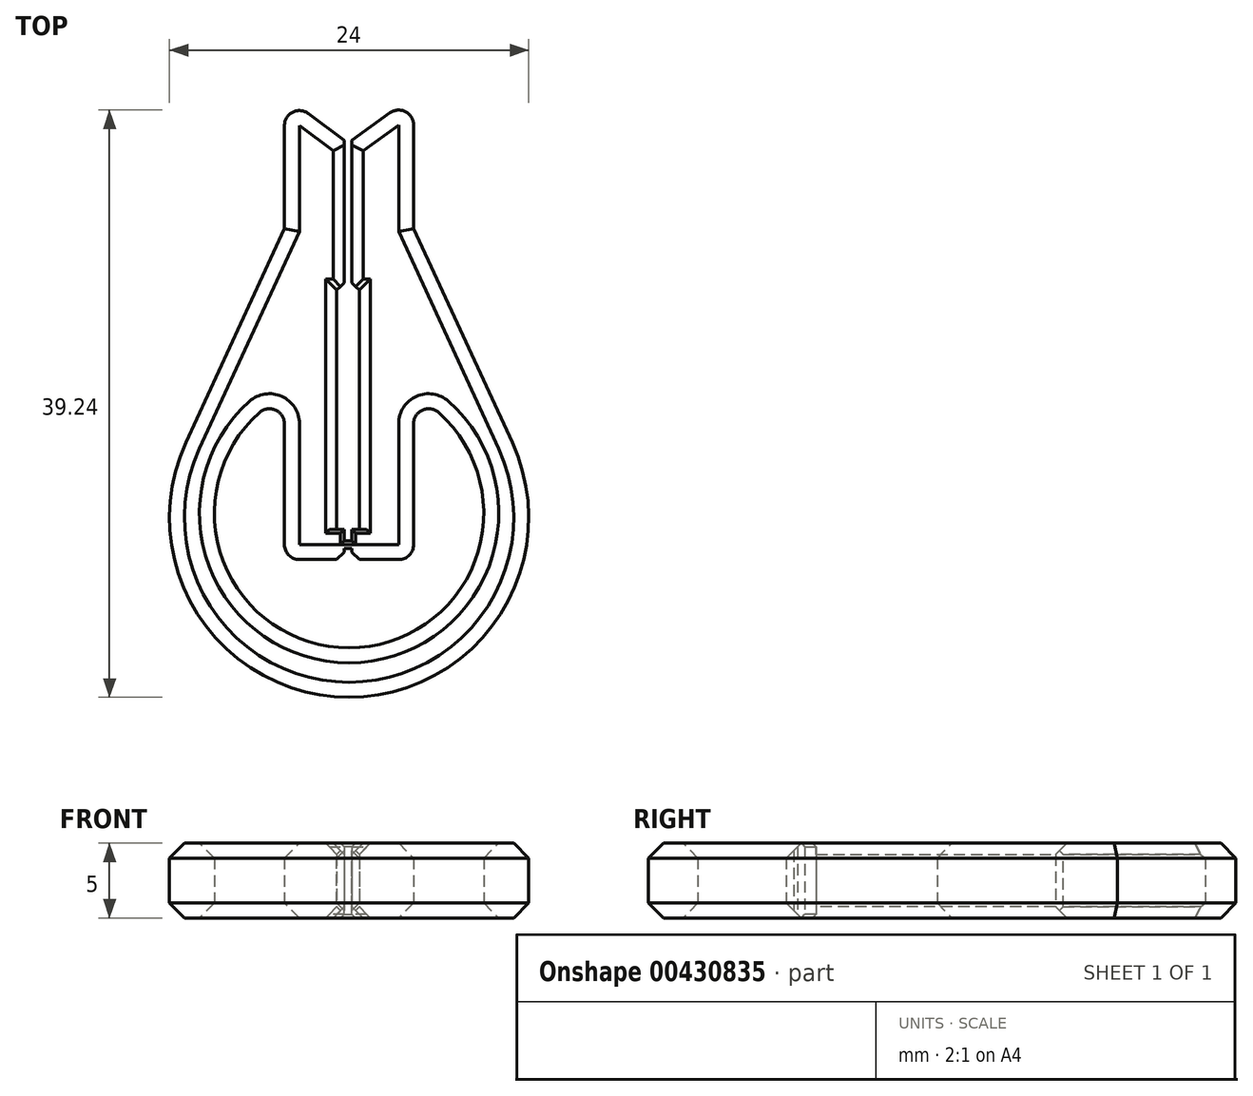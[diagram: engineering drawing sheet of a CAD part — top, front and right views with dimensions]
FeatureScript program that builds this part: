
annotation { "Feature Type Name" : "Feature", "Feature Type Description" : "" }
export const myFeature = defineFeature(function(context is Context, id is Id, definition is map)
    precondition{}
    {
        {
            var Q0;
            Q0=qCreatedBy(makeId("Top.planeOp"),FACE);
            var sketch = newSketch(context, id + "F0", { "sketchPlane" : qUnion([Q0])});
            skLineSegment(sketch, "E0", {"start": v(-0.25, 45.37) * mm, "end": v(-0.25, 35.37) * mm});
            skLineSegment(sketch, "E1", {"start": v(-0.25, 35.37) * mm, "end": v(-0.75, 35.37) * mm});
            skLineSegment(sketch, "E2", {"start": v(-4.25, 17.37) * mm, "end": v(-4.25, 28.37) * mm});
            skLineSegment(sketch, "E3", {"start": v(-4.25, 48.37) * mm, "end": v(-0.25, 45.37) * mm});
            skLineSegment(sketch, "E4", {"start": v(-4.25, 17.37) * mm, "end": v(-0.25, 17.37) * mm});
            skLineSegment(sketch, "E5", {"start": v(-0.25, 17.37) * mm, "end": v(-0.25, 18.12) * mm});
            skLineSegment(sketch, "E6", {"start": v(-0.25, 19.37) * mm, "end": v(-0.75, 19.37) * mm});
            skLineSegment(sketch, "E7", {"start": v(-0.75, 19.37) * mm, "end": v(-0.75, 35.37) * mm});
            skPoint(sketch, "E8", {"position": v(-4.25, 45.37) * mm});
            skPoint(sketch, "E9", {"position": v(-0.25, 18.62) * mm});
            skPoint(sketch, "E10", {"position": v(-0.25, 18.12) * mm});
            skLineSegment(sketch, "E11.MirrorCS", {"start": v(0.25, 19.37) * mm, "end": v(0.75, 19.37) * mm});
            skLineSegment(sketch, "E12.MirrorCS", {"start": v(0.25, 17.37) * mm, "end": v(0.25, 18.12) * mm});
            skPoint(sketch, "E13.MirrorP", {"position": v(0.25, 18.62) * mm});
            skLineSegment(sketch, "E14.MirrorCS", {"start": v(0.25, 35.37) * mm, "end": v(0.75, 35.37) * mm});
            skLineSegment(sketch, "E15.MirrorCS", {"start": v(4.38, 17.37) * mm, "end": v(0.25, 17.37) * mm});
            skPoint(sketch, "E16.MirrorP", {"position": v(0.25, 18.12) * mm});
            skLineSegment(sketch, "E17.MirrorCS", {"start": v(0.75, 19.37) * mm, "end": v(0.75, 35.37) * mm});
            skLineSegment(sketch, "E18.MirrorCS", {"start": v(4.38, 48.37) * mm, "end": v(0.25, 45.37) * mm});
            skLineSegment(sketch, "E19.MirrorCS", {"start": v(4.38, 17.37) * mm, "end": v(4.38, 28.37) * mm});
            skLineSegment(sketch, "E20.MirrorCS", {"start": v(0.25, 45.37) * mm, "end": v(0.25, 35.37) * mm});
            skPoint(sketch, "E21", {"position": v(-4.25, 31.37) * mm});
            skPoint(sketch, "E22", {"position": v(4.38, 31.37) * mm});
            skArc(sketch, "E23", {"start": v(-10.83, 25.2) * mm, "mid": v(0.07, 8.17) * mm, "end": v(10.97, 25.2) * mm});
            skArc(sketch, "E24", {"start": v(-4.25, 28.37) * mm, "mid": v(0.07, 11.47) * mm, "end": v(4.38, 28.37) * mm});
            skLineSegment(sketch, "E25", {"start": v(-4.25, 28.37) * mm, "end": v(4.38, 28.37) * mm, "construction": true});
            skLineSegment(sketch, "E26", {"start": v(-4.25, 31.37) * mm, "end": v(4.38, 31.37) * mm, "construction": true});
            skPoint(sketch, "E27", {"position": v(4.38, 45.37) * mm});
            skLineSegment(sketch, "E28", {"start": v(-0.25, 45.37) * mm, "end": v(0.25, 45.37) * mm, "construction": true});
            skLineSegment(sketch, "E29.trimOffspring", {"start": v(0.25, 18.62) * mm, "end": v(0.25, 19.37) * mm});
            skLineSegment(sketch, "E30.trimOffspring", {"start": v(-0.25, 18.62) * mm, "end": v(-0.25, 19.37) * mm});
            skLineSegment(sketch, "E31", {"start": v(-4.25, 48.37) * mm, "end": v(4.38, 48.37) * mm, "construction": true});
            skLineSegment(sketch, "E32.trimOffspring", {"start": v(-4.25, 31.37) * mm, "end": v(-4.25, 48.37) * mm});
            skLineSegment(sketch, "E33.trimOffspring", {"start": v(4.38, 31.37) * mm, "end": v(4.38, 48.37) * mm});
            skPoint(sketch, "E34", {"position": v(-4.25, 39.5) * mm});
            skPoint(sketch, "E35", {"position": v(4.38, 39.5) * mm});
            skLineSegment(sketch, "E36", {"start": v(-4.25, 39.5) * mm, "end": v(-4.25, 31.37) * mm, "construction": true});
            skLineSegment(sketch, "E37", {"start": v(4.38, 39.5) * mm, "end": v(4.38, 31.37) * mm, "construction": true});
            skLineSegment(sketch, "E38", {"start": v(-4.25, 39.5) * mm, "end": v(-10.83, 25.2) * mm});
            skLineSegment(sketch, "E39", {"start": v(4.38, 39.5) * mm, "end": v(10.97, 25.2) * mm});
            skPoint(sketch, "E40", {"position": v(-10.83, 25.2) * mm});
            skPoint(sketch, "E41", {"position": v(10.97, 25.2) * mm});
            skLineSegment(sketch, "E42", {"start": v(-0.25, 18.62) * mm, "end": v(0, 18.62) * mm});
            skLineSegment(sketch, "E43", {"start": v(-0.25, 18.12) * mm, "end": v(0.25, 18.12) * mm});
            skLineSegment(sketch, "E44", {"start": v(-0.25, 17.37) * mm, "end": v(-0.25, 18.12) * mm, "construction": true});
            skLineSegment(sketch, "E45", {"start": v(-0.25, 19.37) * mm, "end": v(-0.25, 18.62) * mm, "construction": true});
            skLineSegment(sketch, "E46", {"start": v(0, 18.62) * mm, "end": v(0.25, 18.62) * mm});
            skSolve(sketch);
        }
        {
            var Q0;
            Q0=makeQuery(id+"F0.imprint","IMPRINT",FACE,{"disambiguationData":[TD([[makeQuery(id+"F0.imprint","IMPRINT",EDGE,{"derivedFrom":sQuery(id+"F0.wireOp",EDGE,"E0")}),-1.0]])]});
            var Q1;
            Q1=makeQuery(id+"F0.imprint","IMPRINT",FACE,{"disambiguationData":[TD([[makeQuery(id+"F0.imprint","IMPRINT",EDGE,{"derivedFrom":sQuery(id+"F0.wireOp",EDGE,"JaDM6d9C-7Ljt-ahR3-fbqs-DUhw12I5umXE")}),1.0]])]});
            extrude(context, id + "F1", {"entities" : qUnion([Q0, Q1]), "depth" : 5 * mm});
        }
        {
            var Q0;
            Q0=makeQuery(id+"F1.opExtrude","SWEPT_EDGE",EDGE,{"disambiguationData":[OSD([sQuery(id+"F0.wireOp",EDGE,"E3"),sQuery(id+"F0.wireOp",EDGE,"E32.trimOffspring")])]});
            var Q1;
            Q1=makeQuery(id+"F1.opExtrude","SWEPT_EDGE",EDGE,{"disambiguationData":[OSD([sQuery(id+"F0.wireOp",EDGE,"E18.MirrorCS"),sQuery(id+"F0.wireOp",EDGE,"E33.trimOffspring")])]});
            var Q2;
            Q2=makeQuery(id+"F1.opExtrude","SWEPT_EDGE",EDGE,{"disambiguationData":[OSD([sQuery(id+"F0.wireOp",EDGE,"E2"),sQuery(id+"F0.wireOp",EDGE,"E4")])]});
            var Q3;
            Q3=makeQuery(id+"F1.opExtrude","SWEPT_EDGE",EDGE,{"disambiguationData":[OSD([sQuery(id+"F0.wireOp",EDGE,"E15.MirrorCS"),sQuery(id+"F0.wireOp",EDGE,"E19.MirrorCS")])]});
            var Q4;
            Q4=makeQuery(id+"F1.opExtrude","SWEPT_EDGE",EDGE,{"disambiguationData":[OSD([sQuery(id+"F0.wireOp",EDGE,"E19.MirrorCS"),sQuery(id+"F0.wireOp",EDGE,"E24")])]});
            var Q5;
            Q5=makeQuery(id+"F1.opExtrude","SWEPT_EDGE",EDGE,{"disambiguationData":[OSD([sQuery(id+"F0.wireOp",EDGE,"E2"),sQuery(id+"F0.wireOp",EDGE,"E24")])]});
            fillet(context, id + "F2", {"entities" : qUnion([Q0, Q1, Q2, Q3, Q4, Q5]), "radius" : 1 * mm, "tangentPropagation" : true, "allowEdgeOverflow" : false});
        }
        {
            var Q0;
            Q0=makeQuery(id+"F1.opExtrude","CAP_EDGE",EDGE,{"disambiguationData":[OSD([sQuery(id+"F0.wireOp",EDGE,"E43")])],"isStart":false});
            var Q1;
            Q1=makeQuery(id+"F1.opExtrude","CAP_EDGE",EDGE,{"disambiguationData":[OSD([sQuery(id+"F0.wireOp",EDGE,"E42"),sQuery(id+"F0.wireOp",EDGE,"E46")])],"isStart":false});
            var Q2;
            Q2=makeQuery(id+"F1.opExtrude","CAP_EDGE",EDGE,{"disambiguationData":[OSD([sQuery(id+"F0.wireOp",EDGE,"E42"),sQuery(id+"F0.wireOp",EDGE,"E46")])],"isStart":true});
            var Q3;
            Q3=makeQuery(id+"F1.opExtrude","CAP_EDGE",EDGE,{"disambiguationData":[OSD([sQuery(id+"F0.wireOp",EDGE,"E43")])],"isStart":true});
            var Q4;
            Q4=makeQuery(id+"F1.opExtrude","CAP_EDGE",EDGE,{"disambiguationData":[OSD([sQuery(id+"F0.wireOp",EDGE,"E5")])],"isStart":true});
            var Q5;
            Q5=makeQuery(id+"F1.opExtrude","CAP_EDGE",EDGE,{"disambiguationData":[OSD([sQuery(id+"F0.wireOp",EDGE,"E12.MirrorCS")])],"isStart":true});
            var Q6;
            Q6=makeQuery(id+"F1.opExtrude","CAP_EDGE",EDGE,{"disambiguationData":[OSD([sQuery(id+"F0.wireOp",EDGE,"E30.trimOffspring")])],"isStart":true});
            var Q7;
            Q7=makeQuery(id+"F1.opExtrude","CAP_EDGE",EDGE,{"disambiguationData":[OSD([sQuery(id+"F0.wireOp",EDGE,"E29.trimOffspring")])],"isStart":true});
            var Q8;
            Q8=makeQuery(id+"F1.opExtrude","CAP_EDGE",EDGE,{"disambiguationData":[OSD([sQuery(id+"F0.wireOp",EDGE,"E30.trimOffspring")])],"isStart":false});
            var Q9;
            Q9=makeQuery(id+"F1.opExtrude","CAP_EDGE",EDGE,{"disambiguationData":[OSD([sQuery(id+"F0.wireOp",EDGE,"E6")])],"isStart":false});
            var Q10;
            Q10=makeQuery(id+"F1.opExtrude","CAP_EDGE",EDGE,{"disambiguationData":[OSD([sQuery(id+"F0.wireOp",EDGE,"E11.MirrorCS")])],"isStart":false});
            var Q11;
            Q11=makeQuery(id+"F1.opExtrude","CAP_EDGE",EDGE,{"disambiguationData":[OSD([sQuery(id+"F0.wireOp",EDGE,"E29.trimOffspring")])],"isStart":false});
            var Q12;
            Q12=makeQuery(id+"F1.opExtrude","CAP_EDGE",EDGE,{"disambiguationData":[OSD([sQuery(id+"F0.wireOp",EDGE,"E5")])],"isStart":false});
            var Q13;
            Q13=makeQuery(id+"F1.opExtrude","CAP_EDGE",EDGE,{"disambiguationData":[OSD([sQuery(id+"F0.wireOp",EDGE,"E12.MirrorCS")])],"isStart":false});
            var Q14;
            Q14=makeQuery(id+"F1.opExtrude","CAP_EDGE",EDGE,{"disambiguationData":[OSD([sQuery(id+"F0.wireOp",EDGE,"E11.MirrorCS")])],"isStart":true});
            var Q15;
            Q15=makeQuery(id+"F1.opExtrude","CAP_EDGE",EDGE,{"disambiguationData":[OSD([sQuery(id+"F0.wireOp",EDGE,"E6")])],"isStart":true});
            chamfer(context, id + "F3", {"entities" : qUnion([Q0, Q1, Q2, Q3, Q4, Q5, Q6, Q7, Q8, Q9, Q10, Q11, Q12, Q13, Q14, Q15]), "width" : .25 * mm, "tangentPropagation" : true});
        }
        {
            var Q0;
            Q0=makeQuery(id+"F1.opExtrude","CAP_EDGE",EDGE,{"disambiguationData":[OSD([sQuery(id+"F0.wireOp",EDGE,"E32.trimOffspring")])],"isStart":false});
            var Q1;
            Q1=makeQuery(id+"F1.opExtrude","CAP_EDGE",EDGE,{"disambiguationData":[OSD([sQuery(id+"F0.wireOp",EDGE,"E38")])],"isStart":false});
            var Q2;
            Q2=makeQuery(id+"F1.opExtrude","CAP_EDGE",EDGE,{"disambiguationData":[OSD([sQuery(id+"F0.wireOp",EDGE,"E3")])],"isStart":false});
            var Q3;
            Q3=makeQuery(id+"F1.opExtrude","CAP_EDGE",EDGE,{"disambiguationData":[OSD([sQuery(id+"F0.wireOp",EDGE,"E18.MirrorCS")])],"isStart":false});
            var Q4;
            {var subQ0=sQuery(id+"F0.wireOp",EDGE,"E33.trimOffspring");var subQ1=sQuery(id+"F0.wireOp",EDGE,"E18.MirrorCS");Q4=makeQuery(id+"F2.opFillet","BLEND_EDGE",EDGE,{"blendedFrom":[makeQuery(id+"F1.opExtrude","SWEPT_EDGE",EDGE,{"disambiguationData":[OSD([subQ1,subQ0])]}),makeQuery(id+"F1.opExtrude","CAP_FACE",FACE,{"disambiguationData":[OSD([sQuery(id+"F0.wireOp",EDGE,"E0"),sQuery(id+"F0.wireOp",EDGE,"E1"),sQuery(id+"F0.wireOp",EDGE,"E2"),sQuery(id+"F0.wireOp",EDGE,"E3"),sQuery(id+"F0.wireOp",EDGE,"E4"),sQuery(id+"F0.wireOp",EDGE,"E5"),sQuery(id+"F0.wireOp",EDGE,"E6"),sQuery(id+"F0.wireOp",EDGE,"E7"),sQuery(id+"F0.wireOp",EDGE,"E11.MirrorCS"),sQuery(id+"F0.wireOp",EDGE,"E12.MirrorCS"),sQuery(id+"F0.wireOp",EDGE,"E14.MirrorCS"),sQuery(id+"F0.wireOp",EDGE,"E15.MirrorCS"),sQuery(id+"F0.wireOp",EDGE,"E17.MirrorCS"),subQ1,sQuery(id+"F0.wireOp",EDGE,"E19.MirrorCS"),sQuery(id+"F0.wireOp",EDGE,"E20.MirrorCS"),sQuery(id+"F0.wireOp",EDGE,"E23"),sQuery(id+"F0.wireOp",EDGE,"E24"),sQuery(id+"F0.wireOp",EDGE,"E29.trimOffspring"),sQuery(id+"F0.wireOp",EDGE,"E30.trimOffspring"),sQuery(id+"F0.wireOp",EDGE,"E32.trimOffspring"),subQ0,sQuery(id+"F0.wireOp",EDGE,"E38"),sQuery(id+"F0.wireOp",EDGE,"E39"),sQuery(id+"F0.wireOp",EDGE,"E42"),sQuery(id+"F0.wireOp",EDGE,"E43"),sQuery(id+"F0.wireOp",EDGE,"E46")])],"isStart":false})],"blendedInto":[makeQuery(id+"F1.opExtrude","CAP_FACE",FACE,{"disambiguationData":[OSD([sQuery(id+"F0.wireOp",EDGE,"E0"),sQuery(id+"F0.wireOp",EDGE,"E1"),sQuery(id+"F0.wireOp",EDGE,"E2"),sQuery(id+"F0.wireOp",EDGE,"E3"),sQuery(id+"F0.wireOp",EDGE,"E4"),sQuery(id+"F0.wireOp",EDGE,"E5"),sQuery(id+"F0.wireOp",EDGE,"E6"),sQuery(id+"F0.wireOp",EDGE,"E7"),sQuery(id+"F0.wireOp",EDGE,"E11.MirrorCS"),sQuery(id+"F0.wireOp",EDGE,"E12.MirrorCS"),sQuery(id+"F0.wireOp",EDGE,"E14.MirrorCS"),sQuery(id+"F0.wireOp",EDGE,"E15.MirrorCS"),sQuery(id+"F0.wireOp",EDGE,"E17.MirrorCS"),subQ1,sQuery(id+"F0.wireOp",EDGE,"E19.MirrorCS"),sQuery(id+"F0.wireOp",EDGE,"E20.MirrorCS"),sQuery(id+"F0.wireOp",EDGE,"E23"),sQuery(id+"F0.wireOp",EDGE,"E24"),sQuery(id+"F0.wireOp",EDGE,"E29.trimOffspring"),sQuery(id+"F0.wireOp",EDGE,"E30.trimOffspring"),sQuery(id+"F0.wireOp",EDGE,"E32.trimOffspring"),subQ0,sQuery(id+"F0.wireOp",EDGE,"E38"),sQuery(id+"F0.wireOp",EDGE,"E39"),sQuery(id+"F0.wireOp",EDGE,"E42"),sQuery(id+"F0.wireOp",EDGE,"E43"),sQuery(id+"F0.wireOp",EDGE,"E46")])],"isStart":false})]});}
            var Q5;
            Q5=makeQuery(id+"F1.opExtrude","CAP_EDGE",EDGE,{"disambiguationData":[OSD([sQuery(id+"F0.wireOp",EDGE,"E33.trimOffspring")])],"isStart":false});
            var Q6;
            Q6=makeQuery(id+"F1.opExtrude","CAP_EDGE",EDGE,{"disambiguationData":[OSD([sQuery(id+"F0.wireOp",EDGE,"E39")])],"isStart":false});
            var Q7;
            Q7=makeQuery(id+"F1.opExtrude","CAP_EDGE",EDGE,{"disambiguationData":[OSD([sQuery(id+"F0.wireOp",EDGE,"E23")])],"isStart":false});
            var Q8;
            Q8=makeQuery(id+"F1.opExtrude","CAP_EDGE",EDGE,{"disambiguationData":[OSD([sQuery(id+"F0.wireOp",EDGE,"E2")])],"isStart":false});
            var Q9;
            {var subQ0=sQuery(id+"F0.wireOp",EDGE,"E24");var subQ1=sQuery(id+"F0.wireOp",EDGE,"E2");Q9=makeQuery(id+"F2.opFillet","BLEND_EDGE",EDGE,{"blendedFrom":[makeQuery(id+"F1.opExtrude","SWEPT_EDGE",EDGE,{"disambiguationData":[OSD([subQ1,subQ0])]}),makeQuery(id+"F1.opExtrude","CAP_FACE",FACE,{"disambiguationData":[OSD([sQuery(id+"F0.wireOp",EDGE,"E0"),sQuery(id+"F0.wireOp",EDGE,"E1"),subQ1,sQuery(id+"F0.wireOp",EDGE,"E3"),sQuery(id+"F0.wireOp",EDGE,"E4"),sQuery(id+"F0.wireOp",EDGE,"E5"),sQuery(id+"F0.wireOp",EDGE,"E6"),sQuery(id+"F0.wireOp",EDGE,"E7"),sQuery(id+"F0.wireOp",EDGE,"E11.MirrorCS"),sQuery(id+"F0.wireOp",EDGE,"E12.MirrorCS"),sQuery(id+"F0.wireOp",EDGE,"E14.MirrorCS"),sQuery(id+"F0.wireOp",EDGE,"E15.MirrorCS"),sQuery(id+"F0.wireOp",EDGE,"E17.MirrorCS"),sQuery(id+"F0.wireOp",EDGE,"E18.MirrorCS"),sQuery(id+"F0.wireOp",EDGE,"E19.MirrorCS"),sQuery(id+"F0.wireOp",EDGE,"E20.MirrorCS"),sQuery(id+"F0.wireOp",EDGE,"E23"),subQ0,sQuery(id+"F0.wireOp",EDGE,"E29.trimOffspring"),sQuery(id+"F0.wireOp",EDGE,"E30.trimOffspring"),sQuery(id+"F0.wireOp",EDGE,"E32.trimOffspring"),sQuery(id+"F0.wireOp",EDGE,"E33.trimOffspring"),sQuery(id+"F0.wireOp",EDGE,"E38"),sQuery(id+"F0.wireOp",EDGE,"E39"),sQuery(id+"F0.wireOp",EDGE,"E42"),sQuery(id+"F0.wireOp",EDGE,"E43"),sQuery(id+"F0.wireOp",EDGE,"E46")])],"isStart":false})],"blendedInto":[makeQuery(id+"F1.opExtrude","CAP_FACE",FACE,{"disambiguationData":[OSD([sQuery(id+"F0.wireOp",EDGE,"E0"),sQuery(id+"F0.wireOp",EDGE,"E1"),subQ1,sQuery(id+"F0.wireOp",EDGE,"E3"),sQuery(id+"F0.wireOp",EDGE,"E4"),sQuery(id+"F0.wireOp",EDGE,"E5"),sQuery(id+"F0.wireOp",EDGE,"E6"),sQuery(id+"F0.wireOp",EDGE,"E7"),sQuery(id+"F0.wireOp",EDGE,"E11.MirrorCS"),sQuery(id+"F0.wireOp",EDGE,"E12.MirrorCS"),sQuery(id+"F0.wireOp",EDGE,"E14.MirrorCS"),sQuery(id+"F0.wireOp",EDGE,"E15.MirrorCS"),sQuery(id+"F0.wireOp",EDGE,"E17.MirrorCS"),sQuery(id+"F0.wireOp",EDGE,"E18.MirrorCS"),sQuery(id+"F0.wireOp",EDGE,"E19.MirrorCS"),sQuery(id+"F0.wireOp",EDGE,"E20.MirrorCS"),sQuery(id+"F0.wireOp",EDGE,"E23"),subQ0,sQuery(id+"F0.wireOp",EDGE,"E29.trimOffspring"),sQuery(id+"F0.wireOp",EDGE,"E30.trimOffspring"),sQuery(id+"F0.wireOp",EDGE,"E32.trimOffspring"),sQuery(id+"F0.wireOp",EDGE,"E33.trimOffspring"),sQuery(id+"F0.wireOp",EDGE,"E38"),sQuery(id+"F0.wireOp",EDGE,"E39"),sQuery(id+"F0.wireOp",EDGE,"E42"),sQuery(id+"F0.wireOp",EDGE,"E43"),sQuery(id+"F0.wireOp",EDGE,"E46")])],"isStart":false})]});}
            var Q10;
            {var subQ0=sQuery(id+"F0.wireOp",EDGE,"E32.trimOffspring");var subQ1=sQuery(id+"F0.wireOp",EDGE,"E3");Q10=makeQuery(id+"F2.opFillet","BLEND_EDGE",EDGE,{"blendedFrom":[makeQuery(id+"F1.opExtrude","SWEPT_EDGE",EDGE,{"disambiguationData":[OSD([subQ1,subQ0])]}),makeQuery(id+"F1.opExtrude","CAP_FACE",FACE,{"disambiguationData":[OSD([sQuery(id+"F0.wireOp",EDGE,"E0"),sQuery(id+"F0.wireOp",EDGE,"E1"),sQuery(id+"F0.wireOp",EDGE,"E2"),subQ1,sQuery(id+"F0.wireOp",EDGE,"E4"),sQuery(id+"F0.wireOp",EDGE,"E5"),sQuery(id+"F0.wireOp",EDGE,"E6"),sQuery(id+"F0.wireOp",EDGE,"E7"),sQuery(id+"F0.wireOp",EDGE,"E11.MirrorCS"),sQuery(id+"F0.wireOp",EDGE,"E12.MirrorCS"),sQuery(id+"F0.wireOp",EDGE,"E14.MirrorCS"),sQuery(id+"F0.wireOp",EDGE,"E15.MirrorCS"),sQuery(id+"F0.wireOp",EDGE,"E17.MirrorCS"),sQuery(id+"F0.wireOp",EDGE,"E18.MirrorCS"),sQuery(id+"F0.wireOp",EDGE,"E19.MirrorCS"),sQuery(id+"F0.wireOp",EDGE,"E20.MirrorCS"),sQuery(id+"F0.wireOp",EDGE,"E23"),sQuery(id+"F0.wireOp",EDGE,"E24"),sQuery(id+"F0.wireOp",EDGE,"E29.trimOffspring"),sQuery(id+"F0.wireOp",EDGE,"E30.trimOffspring"),subQ0,sQuery(id+"F0.wireOp",EDGE,"E33.trimOffspring"),sQuery(id+"F0.wireOp",EDGE,"E38"),sQuery(id+"F0.wireOp",EDGE,"E39"),sQuery(id+"F0.wireOp",EDGE,"E42"),sQuery(id+"F0.wireOp",EDGE,"E43"),sQuery(id+"F0.wireOp",EDGE,"E46")])],"isStart":false})],"blendedInto":[makeQuery(id+"F1.opExtrude","CAP_FACE",FACE,{"disambiguationData":[OSD([sQuery(id+"F0.wireOp",EDGE,"E0"),sQuery(id+"F0.wireOp",EDGE,"E1"),sQuery(id+"F0.wireOp",EDGE,"E2"),subQ1,sQuery(id+"F0.wireOp",EDGE,"E4"),sQuery(id+"F0.wireOp",EDGE,"E5"),sQuery(id+"F0.wireOp",EDGE,"E6"),sQuery(id+"F0.wireOp",EDGE,"E7"),sQuery(id+"F0.wireOp",EDGE,"E11.MirrorCS"),sQuery(id+"F0.wireOp",EDGE,"E12.MirrorCS"),sQuery(id+"F0.wireOp",EDGE,"E14.MirrorCS"),sQuery(id+"F0.wireOp",EDGE,"E15.MirrorCS"),sQuery(id+"F0.wireOp",EDGE,"E17.MirrorCS"),sQuery(id+"F0.wireOp",EDGE,"E18.MirrorCS"),sQuery(id+"F0.wireOp",EDGE,"E19.MirrorCS"),sQuery(id+"F0.wireOp",EDGE,"E20.MirrorCS"),sQuery(id+"F0.wireOp",EDGE,"E23"),sQuery(id+"F0.wireOp",EDGE,"E24"),sQuery(id+"F0.wireOp",EDGE,"E29.trimOffspring"),sQuery(id+"F0.wireOp",EDGE,"E30.trimOffspring"),subQ0,sQuery(id+"F0.wireOp",EDGE,"E33.trimOffspring"),sQuery(id+"F0.wireOp",EDGE,"E38"),sQuery(id+"F0.wireOp",EDGE,"E39"),sQuery(id+"F0.wireOp",EDGE,"E42"),sQuery(id+"F0.wireOp",EDGE,"E43"),sQuery(id+"F0.wireOp",EDGE,"E46")])],"isStart":false})]});}
            var Q11;
            {var subQ0=sQuery(id+"F0.wireOp",EDGE,"E24");var subQ1=sQuery(id+"F0.wireOp",EDGE,"E19.MirrorCS");Q11=makeQuery(id+"F2.opFillet","BLEND_EDGE",EDGE,{"blendedFrom":[makeQuery(id+"F1.opExtrude","SWEPT_EDGE",EDGE,{"disambiguationData":[OSD([subQ1,subQ0])]}),makeQuery(id+"F1.opExtrude","CAP_FACE",FACE,{"disambiguationData":[OSD([sQuery(id+"F0.wireOp",EDGE,"E0"),sQuery(id+"F0.wireOp",EDGE,"E1"),sQuery(id+"F0.wireOp",EDGE,"E2"),sQuery(id+"F0.wireOp",EDGE,"E3"),sQuery(id+"F0.wireOp",EDGE,"E4"),sQuery(id+"F0.wireOp",EDGE,"E5"),sQuery(id+"F0.wireOp",EDGE,"E6"),sQuery(id+"F0.wireOp",EDGE,"E7"),sQuery(id+"F0.wireOp",EDGE,"E11.MirrorCS"),sQuery(id+"F0.wireOp",EDGE,"E12.MirrorCS"),sQuery(id+"F0.wireOp",EDGE,"E14.MirrorCS"),sQuery(id+"F0.wireOp",EDGE,"E15.MirrorCS"),sQuery(id+"F0.wireOp",EDGE,"E17.MirrorCS"),sQuery(id+"F0.wireOp",EDGE,"E18.MirrorCS"),subQ1,sQuery(id+"F0.wireOp",EDGE,"E20.MirrorCS"),sQuery(id+"F0.wireOp",EDGE,"E23"),subQ0,sQuery(id+"F0.wireOp",EDGE,"E29.trimOffspring"),sQuery(id+"F0.wireOp",EDGE,"E30.trimOffspring"),sQuery(id+"F0.wireOp",EDGE,"E32.trimOffspring"),sQuery(id+"F0.wireOp",EDGE,"E33.trimOffspring"),sQuery(id+"F0.wireOp",EDGE,"E38"),sQuery(id+"F0.wireOp",EDGE,"E39"),sQuery(id+"F0.wireOp",EDGE,"E42"),sQuery(id+"F0.wireOp",EDGE,"E43"),sQuery(id+"F0.wireOp",EDGE,"E46")])],"isStart":false})],"blendedInto":[makeQuery(id+"F1.opExtrude","CAP_FACE",FACE,{"disambiguationData":[OSD([sQuery(id+"F0.wireOp",EDGE,"E0"),sQuery(id+"F0.wireOp",EDGE,"E1"),sQuery(id+"F0.wireOp",EDGE,"E2"),sQuery(id+"F0.wireOp",EDGE,"E3"),sQuery(id+"F0.wireOp",EDGE,"E4"),sQuery(id+"F0.wireOp",EDGE,"E5"),sQuery(id+"F0.wireOp",EDGE,"E6"),sQuery(id+"F0.wireOp",EDGE,"E7"),sQuery(id+"F0.wireOp",EDGE,"E11.MirrorCS"),sQuery(id+"F0.wireOp",EDGE,"E12.MirrorCS"),sQuery(id+"F0.wireOp",EDGE,"E14.MirrorCS"),sQuery(id+"F0.wireOp",EDGE,"E15.MirrorCS"),sQuery(id+"F0.wireOp",EDGE,"E17.MirrorCS"),sQuery(id+"F0.wireOp",EDGE,"E18.MirrorCS"),subQ1,sQuery(id+"F0.wireOp",EDGE,"E20.MirrorCS"),sQuery(id+"F0.wireOp",EDGE,"E23"),subQ0,sQuery(id+"F0.wireOp",EDGE,"E29.trimOffspring"),sQuery(id+"F0.wireOp",EDGE,"E30.trimOffspring"),sQuery(id+"F0.wireOp",EDGE,"E32.trimOffspring"),sQuery(id+"F0.wireOp",EDGE,"E33.trimOffspring"),sQuery(id+"F0.wireOp",EDGE,"E38"),sQuery(id+"F0.wireOp",EDGE,"E39"),sQuery(id+"F0.wireOp",EDGE,"E42"),sQuery(id+"F0.wireOp",EDGE,"E43"),sQuery(id+"F0.wireOp",EDGE,"E46")])],"isStart":false})]});}
            var Q12;
            Q12=makeQuery(id+"F1.opExtrude","CAP_EDGE",EDGE,{"disambiguationData":[OSD([sQuery(id+"F0.wireOp",EDGE,"E19.MirrorCS")])],"isStart":false});
            var Q13;
            Q13=makeQuery(id+"F1.opExtrude","CAP_EDGE",EDGE,{"disambiguationData":[OSD([sQuery(id+"F0.wireOp",EDGE,"E15.MirrorCS")])],"isStart":false});
            var Q14;
            Q14=makeQuery(id+"F1.opExtrude","CAP_EDGE",EDGE,{"disambiguationData":[OSD([sQuery(id+"F0.wireOp",EDGE,"E4")])],"isStart":false});
            var Q15;
            Q15=makeQuery(id+"F1.opExtrude","CAP_EDGE",EDGE,{"disambiguationData":[OSD([sQuery(id+"F0.wireOp",EDGE,"E18.MirrorCS")])],"isStart":true});
            var Q16;
            {var subQ0=sQuery(id+"F0.wireOp",EDGE,"E33.trimOffspring");var subQ1=sQuery(id+"F0.wireOp",EDGE,"E18.MirrorCS");Q16=makeQuery(id+"F2.opFillet","BLEND_EDGE",EDGE,{"blendedFrom":[makeQuery(id+"F1.opExtrude","SWEPT_EDGE",EDGE,{"disambiguationData":[OSD([subQ1,subQ0])]}),makeQuery(id+"F1.opExtrude","CAP_FACE",FACE,{"disambiguationData":[OSD([sQuery(id+"F0.wireOp",EDGE,"E0"),sQuery(id+"F0.wireOp",EDGE,"E1"),sQuery(id+"F0.wireOp",EDGE,"E2"),sQuery(id+"F0.wireOp",EDGE,"E3"),sQuery(id+"F0.wireOp",EDGE,"E4"),sQuery(id+"F0.wireOp",EDGE,"E5"),sQuery(id+"F0.wireOp",EDGE,"E6"),sQuery(id+"F0.wireOp",EDGE,"E7"),sQuery(id+"F0.wireOp",EDGE,"E11.MirrorCS"),sQuery(id+"F0.wireOp",EDGE,"E12.MirrorCS"),sQuery(id+"F0.wireOp",EDGE,"E14.MirrorCS"),sQuery(id+"F0.wireOp",EDGE,"E15.MirrorCS"),sQuery(id+"F0.wireOp",EDGE,"E17.MirrorCS"),subQ1,sQuery(id+"F0.wireOp",EDGE,"E19.MirrorCS"),sQuery(id+"F0.wireOp",EDGE,"E20.MirrorCS"),sQuery(id+"F0.wireOp",EDGE,"E23"),sQuery(id+"F0.wireOp",EDGE,"E24"),sQuery(id+"F0.wireOp",EDGE,"E29.trimOffspring"),sQuery(id+"F0.wireOp",EDGE,"E30.trimOffspring"),sQuery(id+"F0.wireOp",EDGE,"E32.trimOffspring"),subQ0,sQuery(id+"F0.wireOp",EDGE,"E38"),sQuery(id+"F0.wireOp",EDGE,"E39"),sQuery(id+"F0.wireOp",EDGE,"E42"),sQuery(id+"F0.wireOp",EDGE,"E43"),sQuery(id+"F0.wireOp",EDGE,"E46")])],"isStart":true})],"blendedInto":[makeQuery(id+"F1.opExtrude","CAP_FACE",FACE,{"disambiguationData":[OSD([sQuery(id+"F0.wireOp",EDGE,"E0"),sQuery(id+"F0.wireOp",EDGE,"E1"),sQuery(id+"F0.wireOp",EDGE,"E2"),sQuery(id+"F0.wireOp",EDGE,"E3"),sQuery(id+"F0.wireOp",EDGE,"E4"),sQuery(id+"F0.wireOp",EDGE,"E5"),sQuery(id+"F0.wireOp",EDGE,"E6"),sQuery(id+"F0.wireOp",EDGE,"E7"),sQuery(id+"F0.wireOp",EDGE,"E11.MirrorCS"),sQuery(id+"F0.wireOp",EDGE,"E12.MirrorCS"),sQuery(id+"F0.wireOp",EDGE,"E14.MirrorCS"),sQuery(id+"F0.wireOp",EDGE,"E15.MirrorCS"),sQuery(id+"F0.wireOp",EDGE,"E17.MirrorCS"),subQ1,sQuery(id+"F0.wireOp",EDGE,"E19.MirrorCS"),sQuery(id+"F0.wireOp",EDGE,"E20.MirrorCS"),sQuery(id+"F0.wireOp",EDGE,"E23"),sQuery(id+"F0.wireOp",EDGE,"E24"),sQuery(id+"F0.wireOp",EDGE,"E29.trimOffspring"),sQuery(id+"F0.wireOp",EDGE,"E30.trimOffspring"),sQuery(id+"F0.wireOp",EDGE,"E32.trimOffspring"),subQ0,sQuery(id+"F0.wireOp",EDGE,"E38"),sQuery(id+"F0.wireOp",EDGE,"E39"),sQuery(id+"F0.wireOp",EDGE,"E42"),sQuery(id+"F0.wireOp",EDGE,"E43"),sQuery(id+"F0.wireOp",EDGE,"E46")])],"isStart":true})]});}
            var Q17;
            Q17=makeQuery(id+"F1.opExtrude","CAP_EDGE",EDGE,{"disambiguationData":[OSD([sQuery(id+"F0.wireOp",EDGE,"E33.trimOffspring")])],"isStart":true});
            var Q18;
            Q18=makeQuery(id+"F1.opExtrude","CAP_EDGE",EDGE,{"disambiguationData":[OSD([sQuery(id+"F0.wireOp",EDGE,"E39")])],"isStart":true});
            var Q19;
            Q19=makeQuery(id+"F1.opExtrude","CAP_EDGE",EDGE,{"disambiguationData":[OSD([sQuery(id+"F0.wireOp",EDGE,"E23")])],"isStart":true});
            var Q20;
            Q20=makeQuery(id+"F1.opExtrude","CAP_EDGE",EDGE,{"disambiguationData":[OSD([sQuery(id+"F0.wireOp",EDGE,"E38")])],"isStart":true});
            var Q21;
            Q21=makeQuery(id+"F1.opExtrude","CAP_EDGE",EDGE,{"disambiguationData":[OSD([sQuery(id+"F0.wireOp",EDGE,"E32.trimOffspring")])],"isStart":true});
            var Q22;
            Q22=makeQuery(id+"F1.opExtrude","CAP_EDGE",EDGE,{"disambiguationData":[OSD([sQuery(id+"F0.wireOp",EDGE,"E3")])],"isStart":true});
            var Q23;
            {var subQ0=sQuery(id+"F0.wireOp",EDGE,"E32.trimOffspring");var subQ1=sQuery(id+"F0.wireOp",EDGE,"E3");Q23=makeQuery(id+"F2.opFillet","BLEND_EDGE",EDGE,{"blendedFrom":[makeQuery(id+"F1.opExtrude","SWEPT_EDGE",EDGE,{"disambiguationData":[OSD([subQ1,subQ0])]}),makeQuery(id+"F1.opExtrude","CAP_FACE",FACE,{"disambiguationData":[OSD([sQuery(id+"F0.wireOp",EDGE,"E0"),sQuery(id+"F0.wireOp",EDGE,"E1"),sQuery(id+"F0.wireOp",EDGE,"E2"),subQ1,sQuery(id+"F0.wireOp",EDGE,"E4"),sQuery(id+"F0.wireOp",EDGE,"E5"),sQuery(id+"F0.wireOp",EDGE,"E6"),sQuery(id+"F0.wireOp",EDGE,"E7"),sQuery(id+"F0.wireOp",EDGE,"E11.MirrorCS"),sQuery(id+"F0.wireOp",EDGE,"E12.MirrorCS"),sQuery(id+"F0.wireOp",EDGE,"E14.MirrorCS"),sQuery(id+"F0.wireOp",EDGE,"E15.MirrorCS"),sQuery(id+"F0.wireOp",EDGE,"E17.MirrorCS"),sQuery(id+"F0.wireOp",EDGE,"E18.MirrorCS"),sQuery(id+"F0.wireOp",EDGE,"E19.MirrorCS"),sQuery(id+"F0.wireOp",EDGE,"E20.MirrorCS"),sQuery(id+"F0.wireOp",EDGE,"E23"),sQuery(id+"F0.wireOp",EDGE,"E24"),sQuery(id+"F0.wireOp",EDGE,"E29.trimOffspring"),sQuery(id+"F0.wireOp",EDGE,"E30.trimOffspring"),subQ0,sQuery(id+"F0.wireOp",EDGE,"E33.trimOffspring"),sQuery(id+"F0.wireOp",EDGE,"E38"),sQuery(id+"F0.wireOp",EDGE,"E39"),sQuery(id+"F0.wireOp",EDGE,"E42"),sQuery(id+"F0.wireOp",EDGE,"E43"),sQuery(id+"F0.wireOp",EDGE,"E46")])],"isStart":true})],"blendedInto":[makeQuery(id+"F1.opExtrude","CAP_FACE",FACE,{"disambiguationData":[OSD([sQuery(id+"F0.wireOp",EDGE,"E0"),sQuery(id+"F0.wireOp",EDGE,"E1"),sQuery(id+"F0.wireOp",EDGE,"E2"),subQ1,sQuery(id+"F0.wireOp",EDGE,"E4"),sQuery(id+"F0.wireOp",EDGE,"E5"),sQuery(id+"F0.wireOp",EDGE,"E6"),sQuery(id+"F0.wireOp",EDGE,"E7"),sQuery(id+"F0.wireOp",EDGE,"E11.MirrorCS"),sQuery(id+"F0.wireOp",EDGE,"E12.MirrorCS"),sQuery(id+"F0.wireOp",EDGE,"E14.MirrorCS"),sQuery(id+"F0.wireOp",EDGE,"E15.MirrorCS"),sQuery(id+"F0.wireOp",EDGE,"E17.MirrorCS"),sQuery(id+"F0.wireOp",EDGE,"E18.MirrorCS"),sQuery(id+"F0.wireOp",EDGE,"E19.MirrorCS"),sQuery(id+"F0.wireOp",EDGE,"E20.MirrorCS"),sQuery(id+"F0.wireOp",EDGE,"E23"),sQuery(id+"F0.wireOp",EDGE,"E24"),sQuery(id+"F0.wireOp",EDGE,"E29.trimOffspring"),sQuery(id+"F0.wireOp",EDGE,"E30.trimOffspring"),subQ0,sQuery(id+"F0.wireOp",EDGE,"E33.trimOffspring"),sQuery(id+"F0.wireOp",EDGE,"E38"),sQuery(id+"F0.wireOp",EDGE,"E39"),sQuery(id+"F0.wireOp",EDGE,"E42"),sQuery(id+"F0.wireOp",EDGE,"E43"),sQuery(id+"F0.wireOp",EDGE,"E46")])],"isStart":true})]});}
            var Q24;
            {var subQ0=sQuery(id+"F0.wireOp",EDGE,"E24");var subQ1=sQuery(id+"F0.wireOp",EDGE,"E19.MirrorCS");Q24=makeQuery(id+"F2.opFillet","BLEND_EDGE",EDGE,{"blendedFrom":[makeQuery(id+"F1.opExtrude","SWEPT_EDGE",EDGE,{"disambiguationData":[OSD([subQ1,subQ0])]}),makeQuery(id+"F1.opExtrude","CAP_FACE",FACE,{"disambiguationData":[OSD([sQuery(id+"F0.wireOp",EDGE,"E0"),sQuery(id+"F0.wireOp",EDGE,"E1"),sQuery(id+"F0.wireOp",EDGE,"E2"),sQuery(id+"F0.wireOp",EDGE,"E3"),sQuery(id+"F0.wireOp",EDGE,"E4"),sQuery(id+"F0.wireOp",EDGE,"E5"),sQuery(id+"F0.wireOp",EDGE,"E6"),sQuery(id+"F0.wireOp",EDGE,"E7"),sQuery(id+"F0.wireOp",EDGE,"E11.MirrorCS"),sQuery(id+"F0.wireOp",EDGE,"E12.MirrorCS"),sQuery(id+"F0.wireOp",EDGE,"E14.MirrorCS"),sQuery(id+"F0.wireOp",EDGE,"E15.MirrorCS"),sQuery(id+"F0.wireOp",EDGE,"E17.MirrorCS"),sQuery(id+"F0.wireOp",EDGE,"E18.MirrorCS"),subQ1,sQuery(id+"F0.wireOp",EDGE,"E20.MirrorCS"),sQuery(id+"F0.wireOp",EDGE,"E23"),subQ0,sQuery(id+"F0.wireOp",EDGE,"E29.trimOffspring"),sQuery(id+"F0.wireOp",EDGE,"E30.trimOffspring"),sQuery(id+"F0.wireOp",EDGE,"E32.trimOffspring"),sQuery(id+"F0.wireOp",EDGE,"E33.trimOffspring"),sQuery(id+"F0.wireOp",EDGE,"E38"),sQuery(id+"F0.wireOp",EDGE,"E39"),sQuery(id+"F0.wireOp",EDGE,"E42"),sQuery(id+"F0.wireOp",EDGE,"E43"),sQuery(id+"F0.wireOp",EDGE,"E46")])],"isStart":true})],"blendedInto":[makeQuery(id+"F1.opExtrude","CAP_FACE",FACE,{"disambiguationData":[OSD([sQuery(id+"F0.wireOp",EDGE,"E0"),sQuery(id+"F0.wireOp",EDGE,"E1"),sQuery(id+"F0.wireOp",EDGE,"E2"),sQuery(id+"F0.wireOp",EDGE,"E3"),sQuery(id+"F0.wireOp",EDGE,"E4"),sQuery(id+"F0.wireOp",EDGE,"E5"),sQuery(id+"F0.wireOp",EDGE,"E6"),sQuery(id+"F0.wireOp",EDGE,"E7"),sQuery(id+"F0.wireOp",EDGE,"E11.MirrorCS"),sQuery(id+"F0.wireOp",EDGE,"E12.MirrorCS"),sQuery(id+"F0.wireOp",EDGE,"E14.MirrorCS"),sQuery(id+"F0.wireOp",EDGE,"E15.MirrorCS"),sQuery(id+"F0.wireOp",EDGE,"E17.MirrorCS"),sQuery(id+"F0.wireOp",EDGE,"E18.MirrorCS"),subQ1,sQuery(id+"F0.wireOp",EDGE,"E20.MirrorCS"),sQuery(id+"F0.wireOp",EDGE,"E23"),subQ0,sQuery(id+"F0.wireOp",EDGE,"E29.trimOffspring"),sQuery(id+"F0.wireOp",EDGE,"E30.trimOffspring"),sQuery(id+"F0.wireOp",EDGE,"E32.trimOffspring"),sQuery(id+"F0.wireOp",EDGE,"E33.trimOffspring"),sQuery(id+"F0.wireOp",EDGE,"E38"),sQuery(id+"F0.wireOp",EDGE,"E39"),sQuery(id+"F0.wireOp",EDGE,"E42"),sQuery(id+"F0.wireOp",EDGE,"E43"),sQuery(id+"F0.wireOp",EDGE,"E46")])],"isStart":true})]});}
            var Q25;
            Q25=makeQuery(id+"F1.opExtrude","CAP_EDGE",EDGE,{"disambiguationData":[OSD([sQuery(id+"F0.wireOp",EDGE,"E19.MirrorCS")])],"isStart":true});
            var Q26;
            {var subQ0=sQuery(id+"F0.wireOp",EDGE,"E19.MirrorCS");var subQ1=sQuery(id+"F0.wireOp",EDGE,"E15.MirrorCS");Q26=makeQuery(id+"F2.opFillet","BLEND_EDGE",EDGE,{"blendedFrom":[makeQuery(id+"F1.opExtrude","SWEPT_EDGE",EDGE,{"disambiguationData":[OSD([subQ1,subQ0])]}),makeQuery(id+"F1.opExtrude","CAP_FACE",FACE,{"disambiguationData":[OSD([sQuery(id+"F0.wireOp",EDGE,"E0"),sQuery(id+"F0.wireOp",EDGE,"E1"),sQuery(id+"F0.wireOp",EDGE,"E2"),sQuery(id+"F0.wireOp",EDGE,"E3"),sQuery(id+"F0.wireOp",EDGE,"E4"),sQuery(id+"F0.wireOp",EDGE,"E5"),sQuery(id+"F0.wireOp",EDGE,"E6"),sQuery(id+"F0.wireOp",EDGE,"E7"),sQuery(id+"F0.wireOp",EDGE,"E11.MirrorCS"),sQuery(id+"F0.wireOp",EDGE,"E12.MirrorCS"),sQuery(id+"F0.wireOp",EDGE,"E14.MirrorCS"),subQ1,sQuery(id+"F0.wireOp",EDGE,"E17.MirrorCS"),sQuery(id+"F0.wireOp",EDGE,"E18.MirrorCS"),subQ0,sQuery(id+"F0.wireOp",EDGE,"E20.MirrorCS"),sQuery(id+"F0.wireOp",EDGE,"E23"),sQuery(id+"F0.wireOp",EDGE,"E24"),sQuery(id+"F0.wireOp",EDGE,"E29.trimOffspring"),sQuery(id+"F0.wireOp",EDGE,"E30.trimOffspring"),sQuery(id+"F0.wireOp",EDGE,"E32.trimOffspring"),sQuery(id+"F0.wireOp",EDGE,"E33.trimOffspring"),sQuery(id+"F0.wireOp",EDGE,"E38"),sQuery(id+"F0.wireOp",EDGE,"E39"),sQuery(id+"F0.wireOp",EDGE,"E42"),sQuery(id+"F0.wireOp",EDGE,"E43"),sQuery(id+"F0.wireOp",EDGE,"E46")])],"isStart":true})],"blendedInto":[makeQuery(id+"F1.opExtrude","CAP_FACE",FACE,{"disambiguationData":[OSD([sQuery(id+"F0.wireOp",EDGE,"E0"),sQuery(id+"F0.wireOp",EDGE,"E1"),sQuery(id+"F0.wireOp",EDGE,"E2"),sQuery(id+"F0.wireOp",EDGE,"E3"),sQuery(id+"F0.wireOp",EDGE,"E4"),sQuery(id+"F0.wireOp",EDGE,"E5"),sQuery(id+"F0.wireOp",EDGE,"E6"),sQuery(id+"F0.wireOp",EDGE,"E7"),sQuery(id+"F0.wireOp",EDGE,"E11.MirrorCS"),sQuery(id+"F0.wireOp",EDGE,"E12.MirrorCS"),sQuery(id+"F0.wireOp",EDGE,"E14.MirrorCS"),subQ1,sQuery(id+"F0.wireOp",EDGE,"E17.MirrorCS"),sQuery(id+"F0.wireOp",EDGE,"E18.MirrorCS"),subQ0,sQuery(id+"F0.wireOp",EDGE,"E20.MirrorCS"),sQuery(id+"F0.wireOp",EDGE,"E23"),sQuery(id+"F0.wireOp",EDGE,"E24"),sQuery(id+"F0.wireOp",EDGE,"E29.trimOffspring"),sQuery(id+"F0.wireOp",EDGE,"E30.trimOffspring"),sQuery(id+"F0.wireOp",EDGE,"E32.trimOffspring"),sQuery(id+"F0.wireOp",EDGE,"E33.trimOffspring"),sQuery(id+"F0.wireOp",EDGE,"E38"),sQuery(id+"F0.wireOp",EDGE,"E39"),sQuery(id+"F0.wireOp",EDGE,"E42"),sQuery(id+"F0.wireOp",EDGE,"E43"),sQuery(id+"F0.wireOp",EDGE,"E46")])],"isStart":true})]});}
            var Q27;
            {var subQ0=sQuery(id+"F0.wireOp",EDGE,"E24");var subQ1=sQuery(id+"F0.wireOp",EDGE,"E2");Q27=makeQuery(id+"F2.opFillet","BLEND_EDGE",EDGE,{"blendedFrom":[makeQuery(id+"F1.opExtrude","SWEPT_EDGE",EDGE,{"disambiguationData":[OSD([subQ1,subQ0])]}),makeQuery(id+"F1.opExtrude","CAP_FACE",FACE,{"disambiguationData":[OSD([sQuery(id+"F0.wireOp",EDGE,"E0"),sQuery(id+"F0.wireOp",EDGE,"E1"),subQ1,sQuery(id+"F0.wireOp",EDGE,"E3"),sQuery(id+"F0.wireOp",EDGE,"E4"),sQuery(id+"F0.wireOp",EDGE,"E5"),sQuery(id+"F0.wireOp",EDGE,"E6"),sQuery(id+"F0.wireOp",EDGE,"E7"),sQuery(id+"F0.wireOp",EDGE,"E11.MirrorCS"),sQuery(id+"F0.wireOp",EDGE,"E12.MirrorCS"),sQuery(id+"F0.wireOp",EDGE,"E14.MirrorCS"),sQuery(id+"F0.wireOp",EDGE,"E15.MirrorCS"),sQuery(id+"F0.wireOp",EDGE,"E17.MirrorCS"),sQuery(id+"F0.wireOp",EDGE,"E18.MirrorCS"),sQuery(id+"F0.wireOp",EDGE,"E19.MirrorCS"),sQuery(id+"F0.wireOp",EDGE,"E20.MirrorCS"),sQuery(id+"F0.wireOp",EDGE,"E23"),subQ0,sQuery(id+"F0.wireOp",EDGE,"E29.trimOffspring"),sQuery(id+"F0.wireOp",EDGE,"E30.trimOffspring"),sQuery(id+"F0.wireOp",EDGE,"E32.trimOffspring"),sQuery(id+"F0.wireOp",EDGE,"E33.trimOffspring"),sQuery(id+"F0.wireOp",EDGE,"E38"),sQuery(id+"F0.wireOp",EDGE,"E39"),sQuery(id+"F0.wireOp",EDGE,"E42"),sQuery(id+"F0.wireOp",EDGE,"E43"),sQuery(id+"F0.wireOp",EDGE,"E46")])],"isStart":true})],"blendedInto":[makeQuery(id+"F1.opExtrude","CAP_FACE",FACE,{"disambiguationData":[OSD([sQuery(id+"F0.wireOp",EDGE,"E0"),sQuery(id+"F0.wireOp",EDGE,"E1"),subQ1,sQuery(id+"F0.wireOp",EDGE,"E3"),sQuery(id+"F0.wireOp",EDGE,"E4"),sQuery(id+"F0.wireOp",EDGE,"E5"),sQuery(id+"F0.wireOp",EDGE,"E6"),sQuery(id+"F0.wireOp",EDGE,"E7"),sQuery(id+"F0.wireOp",EDGE,"E11.MirrorCS"),sQuery(id+"F0.wireOp",EDGE,"E12.MirrorCS"),sQuery(id+"F0.wireOp",EDGE,"E14.MirrorCS"),sQuery(id+"F0.wireOp",EDGE,"E15.MirrorCS"),sQuery(id+"F0.wireOp",EDGE,"E17.MirrorCS"),sQuery(id+"F0.wireOp",EDGE,"E18.MirrorCS"),sQuery(id+"F0.wireOp",EDGE,"E19.MirrorCS"),sQuery(id+"F0.wireOp",EDGE,"E20.MirrorCS"),sQuery(id+"F0.wireOp",EDGE,"E23"),subQ0,sQuery(id+"F0.wireOp",EDGE,"E29.trimOffspring"),sQuery(id+"F0.wireOp",EDGE,"E30.trimOffspring"),sQuery(id+"F0.wireOp",EDGE,"E32.trimOffspring"),sQuery(id+"F0.wireOp",EDGE,"E33.trimOffspring"),sQuery(id+"F0.wireOp",EDGE,"E38"),sQuery(id+"F0.wireOp",EDGE,"E39"),sQuery(id+"F0.wireOp",EDGE,"E42"),sQuery(id+"F0.wireOp",EDGE,"E43"),sQuery(id+"F0.wireOp",EDGE,"E46")])],"isStart":true})]});}
            var Q28;
            Q28=makeQuery(id+"F1.opExtrude","CAP_EDGE",EDGE,{"disambiguationData":[OSD([sQuery(id+"F0.wireOp",EDGE,"E2")])],"isStart":true});
            var Q29;
            {var subQ0=sQuery(id+"F0.wireOp",EDGE,"E4");var subQ1=sQuery(id+"F0.wireOp",EDGE,"E2");Q29=makeQuery(id+"F2.opFillet","BLEND_EDGE",EDGE,{"blendedFrom":[makeQuery(id+"F1.opExtrude","SWEPT_EDGE",EDGE,{"disambiguationData":[OSD([subQ1,subQ0])]}),makeQuery(id+"F1.opExtrude","CAP_FACE",FACE,{"disambiguationData":[OSD([sQuery(id+"F0.wireOp",EDGE,"E0"),sQuery(id+"F0.wireOp",EDGE,"E1"),subQ1,sQuery(id+"F0.wireOp",EDGE,"E3"),subQ0,sQuery(id+"F0.wireOp",EDGE,"E5"),sQuery(id+"F0.wireOp",EDGE,"E6"),sQuery(id+"F0.wireOp",EDGE,"E7"),sQuery(id+"F0.wireOp",EDGE,"E11.MirrorCS"),sQuery(id+"F0.wireOp",EDGE,"E12.MirrorCS"),sQuery(id+"F0.wireOp",EDGE,"E14.MirrorCS"),sQuery(id+"F0.wireOp",EDGE,"E15.MirrorCS"),sQuery(id+"F0.wireOp",EDGE,"E17.MirrorCS"),sQuery(id+"F0.wireOp",EDGE,"E18.MirrorCS"),sQuery(id+"F0.wireOp",EDGE,"E19.MirrorCS"),sQuery(id+"F0.wireOp",EDGE,"E20.MirrorCS"),sQuery(id+"F0.wireOp",EDGE,"E23"),sQuery(id+"F0.wireOp",EDGE,"E24"),sQuery(id+"F0.wireOp",EDGE,"E29.trimOffspring"),sQuery(id+"F0.wireOp",EDGE,"E30.trimOffspring"),sQuery(id+"F0.wireOp",EDGE,"E32.trimOffspring"),sQuery(id+"F0.wireOp",EDGE,"E33.trimOffspring"),sQuery(id+"F0.wireOp",EDGE,"E38"),sQuery(id+"F0.wireOp",EDGE,"E39"),sQuery(id+"F0.wireOp",EDGE,"E42"),sQuery(id+"F0.wireOp",EDGE,"E43"),sQuery(id+"F0.wireOp",EDGE,"E46")])],"isStart":true})],"blendedInto":[makeQuery(id+"F1.opExtrude","CAP_FACE",FACE,{"disambiguationData":[OSD([sQuery(id+"F0.wireOp",EDGE,"E0"),sQuery(id+"F0.wireOp",EDGE,"E1"),subQ1,sQuery(id+"F0.wireOp",EDGE,"E3"),subQ0,sQuery(id+"F0.wireOp",EDGE,"E5"),sQuery(id+"F0.wireOp",EDGE,"E6"),sQuery(id+"F0.wireOp",EDGE,"E7"),sQuery(id+"F0.wireOp",EDGE,"E11.MirrorCS"),sQuery(id+"F0.wireOp",EDGE,"E12.MirrorCS"),sQuery(id+"F0.wireOp",EDGE,"E14.MirrorCS"),sQuery(id+"F0.wireOp",EDGE,"E15.MirrorCS"),sQuery(id+"F0.wireOp",EDGE,"E17.MirrorCS"),sQuery(id+"F0.wireOp",EDGE,"E18.MirrorCS"),sQuery(id+"F0.wireOp",EDGE,"E19.MirrorCS"),sQuery(id+"F0.wireOp",EDGE,"E20.MirrorCS"),sQuery(id+"F0.wireOp",EDGE,"E23"),sQuery(id+"F0.wireOp",EDGE,"E24"),sQuery(id+"F0.wireOp",EDGE,"E29.trimOffspring"),sQuery(id+"F0.wireOp",EDGE,"E30.trimOffspring"),sQuery(id+"F0.wireOp",EDGE,"E32.trimOffspring"),sQuery(id+"F0.wireOp",EDGE,"E33.trimOffspring"),sQuery(id+"F0.wireOp",EDGE,"E38"),sQuery(id+"F0.wireOp",EDGE,"E39"),sQuery(id+"F0.wireOp",EDGE,"E42"),sQuery(id+"F0.wireOp",EDGE,"E43"),sQuery(id+"F0.wireOp",EDGE,"E46")])],"isStart":true})]});}
            var Q30;
            Q30=makeQuery(id+"F1.opExtrude","CAP_EDGE",EDGE,{"disambiguationData":[OSD([sQuery(id+"F0.wireOp",EDGE,"E4")])],"isStart":true});
            var Q31;
            Q31=makeQuery(id+"F1.opExtrude","CAP_EDGE",EDGE,{"disambiguationData":[OSD([sQuery(id+"F0.wireOp",EDGE,"E15.MirrorCS")])],"isStart":true});
            var Q32;
            Q32=makeQuery(id+"F1.opExtrude","CAP_EDGE",EDGE,{"disambiguationData":[OSD([sQuery(id+"F0.wireOp",EDGE,"E24")])],"isStart":false});
            var Q33;
            Q33=makeQuery(id+"F1.opExtrude","CAP_EDGE",EDGE,{"disambiguationData":[OSD([sQuery(id+"F0.wireOp",EDGE,"E24")])],"isStart":true});
            chamfer(context, id + "F4", {"entities" : qUnion([Q0, Q1, Q2, Q3, Q4, Q5, Q6, Q7, Q8, Q9, Q10, Q11, Q12, Q13, Q14, Q15, Q16, Q17, Q18, Q19, Q20, Q21, Q22, Q23, Q24, Q25, Q26, Q27, Q28, Q29, Q30, Q31, Q32, Q33]), "width" : 1 * mm});
        }
        {
            var Q0;
            Q0=makeQuery(id+"F1.opExtrude","CAP_EDGE",EDGE,{"disambiguationData":[OSD([sQuery(id+"F0.wireOp",EDGE,"E0")])],"isStart":false});
            var Q1;
            Q1=makeQuery(id+"F1.opExtrude","CAP_EDGE",EDGE,{"disambiguationData":[OSD([sQuery(id+"F0.wireOp",EDGE,"E20.MirrorCS")])],"isStart":false});
            var Q2;
            Q2=makeQuery(id+"F1.opExtrude","CAP_EDGE",EDGE,{"disambiguationData":[OSD([sQuery(id+"F0.wireOp",EDGE,"E7")])],"isStart":false});
            var Q3;
            Q3=makeQuery(id+"F1.opExtrude","CAP_EDGE",EDGE,{"disambiguationData":[OSD([sQuery(id+"F0.wireOp",EDGE,"E17.MirrorCS")])],"isStart":false});
            var Q4;
            Q4=makeQuery(id+"F1.opExtrude","CAP_EDGE",EDGE,{"disambiguationData":[OSD([sQuery(id+"F0.wireOp",EDGE,"E14.MirrorCS")])],"isStart":false});
            var Q5;
            Q5=makeQuery(id+"F1.opExtrude","CAP_EDGE",EDGE,{"disambiguationData":[OSD([sQuery(id+"F0.wireOp",EDGE,"E1")])],"isStart":false});
            var Q6;
            Q6=makeQuery(id+"F1.opExtrude","CAP_EDGE",EDGE,{"disambiguationData":[OSD([sQuery(id+"F0.wireOp",EDGE,"E17.MirrorCS")])],"isStart":true});
            var Q7;
            Q7=makeQuery(id+"F1.opExtrude","CAP_EDGE",EDGE,{"disambiguationData":[OSD([sQuery(id+"F0.wireOp",EDGE,"E7")])],"isStart":true});
            var Q8;
            Q8=makeQuery(id+"F1.opExtrude","CAP_EDGE",EDGE,{"disambiguationData":[OSD([sQuery(id+"F0.wireOp",EDGE,"E0")])],"isStart":true});
            var Q9;
            Q9=makeQuery(id+"F1.opExtrude","CAP_EDGE",EDGE,{"disambiguationData":[OSD([sQuery(id+"F0.wireOp",EDGE,"E20.MirrorCS")])],"isStart":true});
            var Q10;
            Q10=makeQuery(id+"F1.opExtrude","CAP_EDGE",EDGE,{"disambiguationData":[OSD([sQuery(id+"F0.wireOp",EDGE,"E1")])],"isStart":true});
            var Q11;
            Q11=makeQuery(id+"F1.opExtrude","CAP_EDGE",EDGE,{"disambiguationData":[OSD([sQuery(id+"F0.wireOp",EDGE,"E14.MirrorCS")])],"isStart":true});
            chamfer(context, id + "F5", {"entities" : qUnion([Q0, Q1, Q2, Q3, Q4, Q5, Q6, Q7, Q8, Q9, Q10, Q11]), "width" : .75 * mm, "tangentPropagation" : true});
        }
        {
            var Q0;
            Q0=makeQuery(id+"F1.opExtrude","SWEPT_EDGE",EDGE,{"disambiguationData":[OSD([sQuery(id+"F0.wireOp",EDGE,"E12.MirrorCS"),sQuery(id+"F0.wireOp",EDGE,"E15.MirrorCS")])]});
            var Q1;
            Q1=makeQuery(id+"F1.opExtrude","SWEPT_EDGE",EDGE,{"disambiguationData":[OSD([sQuery(id+"F0.wireOp",EDGE,"E4"),sQuery(id+"F0.wireOp",EDGE,"E5")])]});
            var Q2;
            Q2=makeQuery(id+"F1.opExtrude","SWEPT_EDGE",EDGE,{"disambiguationData":[OSD([sQuery(id+"F0.wireOp",EDGE,"E0"),sQuery(id+"F0.wireOp",EDGE,"E1")])]});
            var Q3;
            Q3=makeQuery(id+"F1.opExtrude","SWEPT_EDGE",EDGE,{"disambiguationData":[OSD([sQuery(id+"F0.wireOp",EDGE,"E14.MirrorCS"),sQuery(id+"F0.wireOp",EDGE,"E20.MirrorCS")])]});
            chamfer(context, id + "F6", {"entities" : qUnion([Q0, Q1, Q2, Q3]), "width" : .5 * mm, "tangentPropagation" : true});
        }
    });
